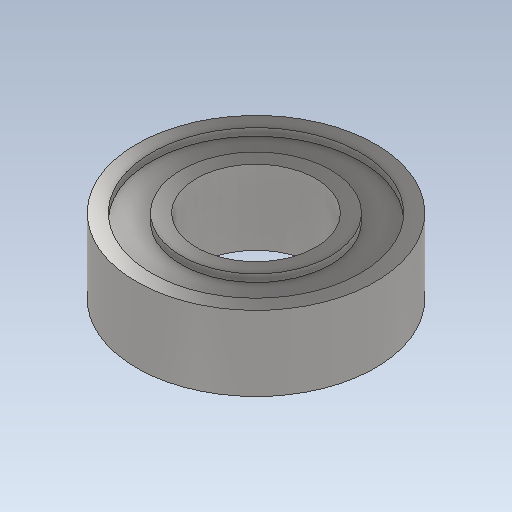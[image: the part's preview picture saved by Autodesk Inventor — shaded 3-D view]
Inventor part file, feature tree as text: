
AUTODESK INVENTOR PART (.ipt)
format: ipt  version: 2020 (Build 240168000, 168)  size: 162,816 bytes
history: native  units: mm
features: extrude x3, sketch x3, projected_geometry x1
ambient origin geometry x8: Origin, YZ Plane, XZ Plane, XY Plane, X Axis, Y Axis, Z Axis, Center Point
bodies: Solid1 (feature_tree)
feature tree (7):
  extrude  "Extrusion1"  Depth=8.0mm
  extrude  "Extrusion2"  Depth=10.0mm
  extrude  "Extrusion3"  Depth=0.5mm TaperAngle=0.0deg
  sketch  "Sketch1"  dims[d0=8.0mm d1=16.0mm]
  sketch  "Sketch2"  dims[d2=5.0mm d3=0.0mm d4=10.0mm]
  projected_geometry  "Projected Loop1"
  sketch  "Sketch3"  dims[d5=14.0mm d6=0.5mm d7=0.0mm d8=0.5mm d9=0.0mm]
